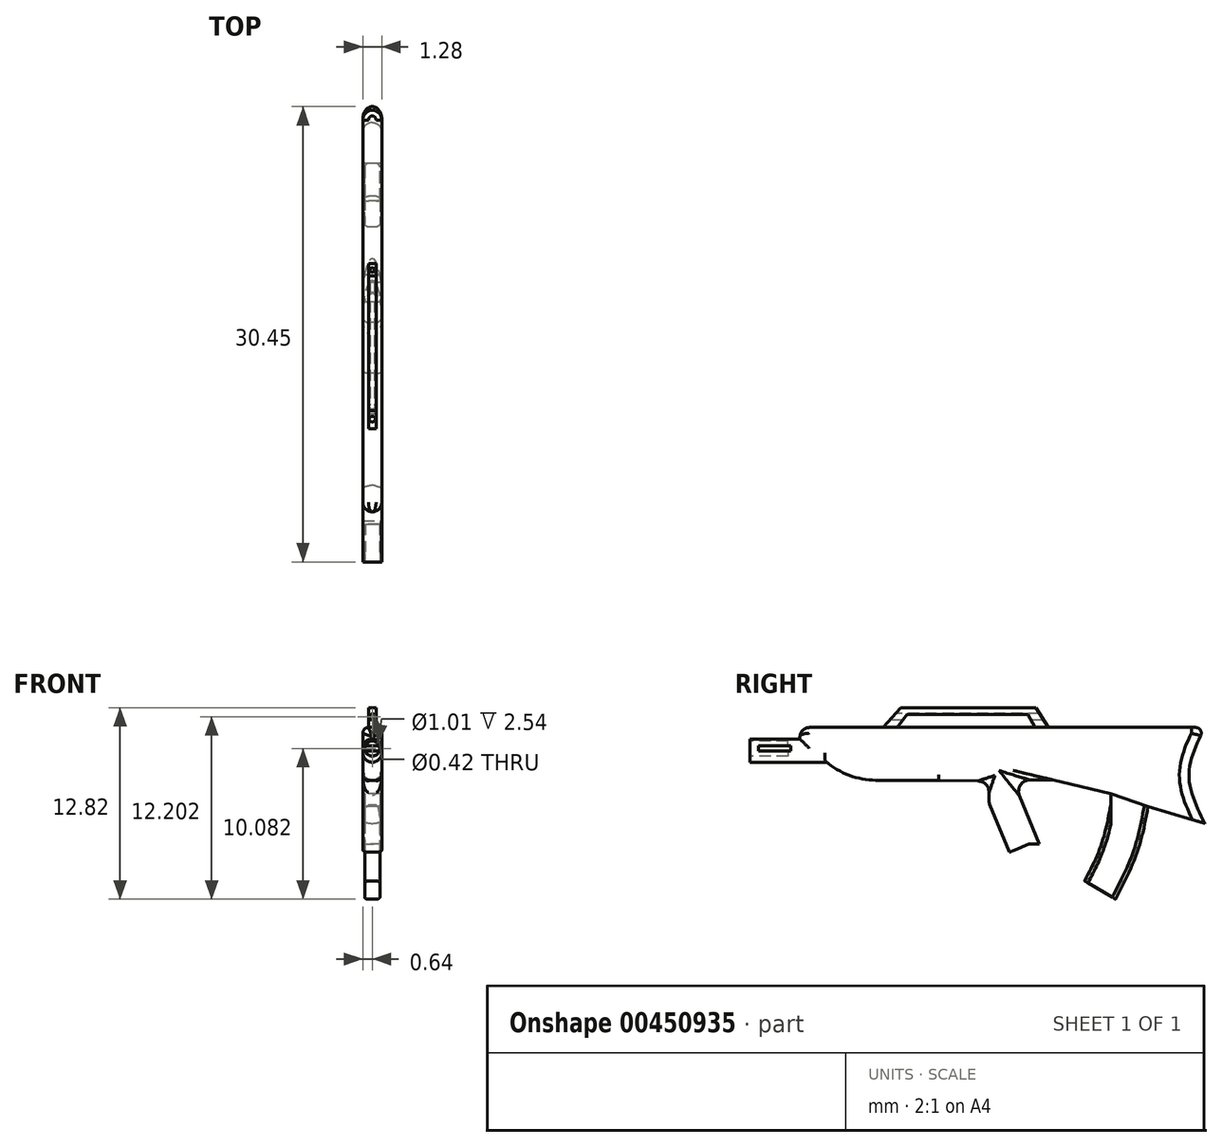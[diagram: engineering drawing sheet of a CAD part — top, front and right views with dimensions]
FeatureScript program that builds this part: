
annotation { "Feature Type Name" : "Feature", "Feature Type Description" : "" }
export const myFeature = defineFeature(function(context is Context, id is Id, definition is map)
    precondition{}
    {
        {
            var Q0;
            Q0=qCreatedBy(makeId("Right.planeOp"),FACE);
            var sketch = newSketch(context, id + "F0", { "sketchPlane" : qUnion([Q0])});
            skLineSegment(sketch, "E0", {"start": v(0, 0) * mm, "end": v(27.1, 0) * mm});
            skFitSpline(sketch, "E1", {"points": [v(27.1, 0) * mm, v(26.04, -3.17) * mm, v(27.1, -6.42) * mm], "startDerivative": vector(-3.2, -6.36) * mm, "endDerivative": vector(3.2, -6.47) * mm});
            skLineSegment(sketch, "E2", {"start": v(27.1, -6.42) * mm, "end": v(23.3, -5.3) * mm});
            skFitSpline(sketch, "E3", {"points": [v(23.3, -5.3) * mm, v(22.6, -8.28) * mm, v(21.12, -11.49) * mm], "startDerivative": vector(-1.13, -6.19) * mm, "endDerivative": vector(-3.2, -6.2) * mm});
            skLineSegment(sketch, "E4", {"start": v(0, 0) * mm, "end": v(0, -0.77) * mm});
            skLineSegment(sketch, "E5", {"start": v(0, -0.77) * mm, "end": v(-3.35, -0.77) * mm});
            skLineSegment(sketch, "E6", {"start": v(-3.35, -0.77) * mm, "end": v(-3.35, -1.64) * mm});
            skLineSegment(sketch, "E7", {"start": v(-3.35, -1.64) * mm, "end": v(-3.35, -2.33) * mm});
            skLineSegment(sketch, "E8", {"start": v(-3.35, -2.33) * mm, "end": v(0, -2.33) * mm});
            skLineSegment(sketch, "E9", {"start": v(0, -2.33) * mm, "end": v(0, -3.53) * mm});
            skLineSegment(sketch, "E10", {"start": v(0, -3.53) * mm, "end": v(9.29, -3.53) * mm});
            skLineSegment(sketch, "E11", {"start": v(9.29, -3.53) * mm, "end": v(10.23, -5.06) * mm});
            skLineSegment(sketch, "E12", {"start": v(10.23, -5.06) * mm, "end": v(12.67, -5.06) * mm});
            skLineSegment(sketch, "E13", {"start": v(12.67, -5.06) * mm, "end": v(12.67, -3.58) * mm});
            skLineSegment(sketch, "E14", {"start": v(12.67, -3.58) * mm, "end": v(9.29, -3.53) * mm});
            skLineSegment(sketch, "E15", {"start": v(12.67, -5.06) * mm, "end": v(14.02, -8.34) * mm});
            skLineSegment(sketch, "E16", {"start": v(14.02, -8.34) * mm, "end": v(15.35, -7.8) * mm});
            skLineSegment(sketch, "E17", {"start": v(15.35, -7.8) * mm, "end": v(13.58, -3.51) * mm});
            skLineSegment(sketch, "E18", {"start": v(13.58, -3.51) * mm, "end": v(12.67, -3.58) * mm});
            skLineSegment(sketch, "E19", {"start": v(21.12, -11.49) * mm, "end": v(19.06, -10.27) * mm});
            skFitSpline(sketch, "E20", {"points": [v(19.06, -10.27) * mm, v(20.18, -7.83) * mm, v(20.8, -5.2) * mm], "startDerivative": vector(2.5, 4.8) * mm, "endDerivative": vector(1, 5.35) * mm});
            skLineSegment(sketch, "E21", {"start": v(13.58, -3.51) * mm, "end": v(16.95, -3.51) * mm});
            skLineSegment(sketch, "E22", {"start": v(16.95, -3.51) * mm, "end": v(20.8, -4.43) * mm});
            skLineSegment(sketch, "E23", {"start": v(20.8, -4.43) * mm, "end": v(20.8, -5.2) * mm});
            skLineSegment(sketch, "E24", {"start": v(14.26, -3.51) * mm, "end": v(16, -7.8) * mm});
            skLineSegment(sketch, "E25", {"start": v(16, -7.8) * mm, "end": v(15.35, -7.8) * mm});
            skLineSegment(sketch, "E26", {"start": v(16.62, 0) * mm, "end": v(15.8, 1.33) * mm});
            skLineSegment(sketch, "E27", {"start": v(15.8, 1.33) * mm, "end": v(6.75, 1.33) * mm});
            skLineSegment(sketch, "E28", {"start": v(6.75, 1.33) * mm, "end": v(5.57, 0) * mm});
            skLineSegment(sketch, "E29", {"start": v(0.72, 0) * mm, "end": v(0.72, 1.2) * mm});
            skLineSegment(sketch, "E30", {"start": v(0.72, 1.2) * mm, "end": v(0.72, 1.86) * mm});
            skLineSegment(sketch, "E31", {"start": v(0.72, 1.86) * mm, "end": v(2.07, 0) * mm});
            skLineSegment(sketch, "E32", {"start": v(20.8, -4.43) * mm, "end": v(23.3, -5.3) * mm});
            skFitSpline(sketch, "E33", {"points": [v(11.82, -3.57) * mm, v(11.61, -4.19) * mm, v(11.17, -4.73) * mm, v(11.36, -4.1) * mm, v(11.35, -3.56) * mm], "startDerivative": vector(-0.42, -2.2) * mm, "endDerivative": vector(-0.44, 2) * mm});
            skLineSegment(sketch, "E34", {"start": v(12.75, -5.25) * mm, "end": v(10.16, -5.25) * mm});
            skLineSegment(sketch, "E35", {"start": v(10.16, -5.25) * mm, "end": v(9.1, -3.53) * mm});
            skLineSegment(sketch, "E36", {"start": v(6.53, 0) * mm, "end": v(7.15, 0.87) * mm});
            skLineSegment(sketch, "E37", {"start": v(7.15, 0.87) * mm, "end": v(15.25, 0.87) * mm});
            skLineSegment(sketch, "E38", {"start": v(15.25, 0.87) * mm, "end": v(15.73, 0) * mm});
            skSolve(sketch);
        }
        {
            var Q0;
            {var subQ18=sQuery(id+"F0.wireOp",EDGE,"E1");Q0=makeQuery(id+"F0.imprint","IMPRINT",FACE,{"disambiguationData":[TD([[makeQuery(id+"F0.imprint","IMPRINT",EDGE,{"derivedFrom":subQ18}),-1.0]])]});}
            var Q1;
            {var subQ0=sQuery(id+"F0.wireOp",EDGE,"E17");Q1=makeQuery(id+"F0.imprint","IMPRINT",FACE,{"disambiguationData":[TD([[makeQuery(id+"F0.imprint","IMPRINT",EDGE,{"derivedFrom":subQ0}),-1.0]])]});}
            var Q2;
            {var subQ2=sQuery(id+"F0.wireOp",EDGE,"E13");Q2=makeQuery(id+"F0.imprint","IMPRINT",FACE,{"disambiguationData":[TD([[makeQuery(id+"F0.imprint","IMPRINT",EDGE,{"derivedFrom":subQ2}),-1.0]])]});}
            extrude(context, id + "F1", {"entities" : qUnion([Q0, Q1, Q2]), "depth" : 0.64 * mm});
        }
        {
            var Q0;
            {var subQ18=sQuery(id+"F0.wireOp",EDGE,"E1");Q0=makeQuery(id+"F0.imprint","IMPRINT",FACE,{"disambiguationData":[TD([[makeQuery(id+"F0.imprint","IMPRINT",EDGE,{"derivedFrom":subQ18}),-1.0]])]});}
            var Q1;
            {var subQ0=sQuery(id+"F0.wireOp",EDGE,"E17");Q1=makeQuery(id+"F0.imprint","IMPRINT",FACE,{"disambiguationData":[TD([[makeQuery(id+"F0.imprint","IMPRINT",EDGE,{"derivedFrom":subQ0}),-1.0]])]});}
            var Q2;
            {var subQ2=sQuery(id+"F0.wireOp",EDGE,"E13");Q2=makeQuery(id+"F0.imprint","IMPRINT",FACE,{"disambiguationData":[TD([[makeQuery(id+"F0.imprint","IMPRINT",EDGE,{"derivedFrom":subQ2}),-1.0]])]});}
            extrude(context, id + "F2", {"entities" : qUnion([Q0, Q1, Q2]), "operationType" : NewBodyOperationType.ADD, "oppositeDirection" : true, "depth" : 0.64 * mm});
        }
        {
            var Q0;
            Q0=makeQuery(id+"F2.opExtrude","CAP_EDGE",EDGE,{"disambiguationData":[OSD([sQuery(id+"F0.wireOp",EDGE,"E5")])],"isStart":false});
            var Q1;
            Q1=makeQuery(id+"F1.opExtrude","CAP_EDGE",EDGE,{"disambiguationData":[OSD([sQuery(id+"F0.wireOp",EDGE,"E5")])],"isStart":false});
            var Q2;
            Q2=makeQuery(id+"F1.opExtrude","CAP_EDGE",EDGE,{"disambiguationData":[OSD([sQuery(id+"F0.wireOp",EDGE,"E8")])],"isStart":false});
            var Q3;
            Q3=makeQuery(id+"F2.opExtrude","CAP_EDGE",EDGE,{"disambiguationData":[OSD([sQuery(id+"F0.wireOp",EDGE,"E8")])],"isStart":false});
            fillet(context, id + "F3", {"entities" : qUnion([Q0, Q1, Q2, Q3]), "radius" : 0.64 * mm, "tangentPropagation" : true, "allowEdgeOverflow" : false});
        }
        {
            var Q0;
            {var subQ0=sQuery(id+"F0.wireOp",EDGE,"E10");var subQ1=sQuery(id+"F0.wireOp",EDGE,"E9");Q0=makeQuery(id+"F2.boolean.opBoolean","MERGE",EDGE,{"derivedFrom":[makeQuery(id+"F1.opExtrude","SWEPT_EDGE",EDGE,{"disambiguationData":[OSD([subQ1,subQ0])]}),makeQuery(id+"F2.opExtrude","SWEPT_EDGE",EDGE,{"disambiguationData":[OSD([subQ1,subQ0])]})]});}
            fillet(context, id + "F4", {"entities" : qUnion([Q0]), "radius" : 5.08 * mm, "tangentPropagation" : true, "allowEdgeOverflow" : false});
        }
        {
            var Q0;
            Q0=makeQuery(id+"F2.opExtrude","CAP_EDGE",EDGE,{"disambiguationData":[OSD([sQuery(id+"F0.wireOp",EDGE,"E24")])],"isStart":false});
            var Q1;
            Q1=makeQuery(id+"F1.opExtrude","CAP_EDGE",EDGE,{"disambiguationData":[OSD([sQuery(id+"F0.wireOp",EDGE,"E24")])],"isStart":false});
            var Q2;
            Q2=makeQuery(id+"F2.opExtrude","CAP_EDGE",EDGE,{"disambiguationData":[OSD([sQuery(id+"F0.wireOp",EDGE,"E1")])],"isStart":false});
            var Q3;
            Q3=makeQuery(id+"F1.opExtrude","CAP_EDGE",EDGE,{"disambiguationData":[OSD([sQuery(id+"F0.wireOp",EDGE,"E1")])],"isStart":false});
            var Q4;
            {var subQ0=sQuery(id+"F0.wireOp",EDGE,"E4");var subQ1=sQuery(id+"F0.wireOp",EDGE,"E0");Q4=makeQuery(id+"F2.boolean.opBoolean","MERGE",EDGE,{"derivedFrom":[makeQuery(id+"F1.opExtrude","SWEPT_EDGE",EDGE,{"disambiguationData":[OSD([subQ1,subQ0])]}),makeQuery(id+"F2.opExtrude","SWEPT_EDGE",EDGE,{"disambiguationData":[OSD([subQ1,subQ0])]})]});}
            var Q5;
            Q5=makeQuery(id+"F1.opExtrude","CAP_EDGE",EDGE,{"disambiguationData":[OSD([sQuery(id+"F0.wireOp",EDGE,"E4")])],"isStart":false});
            var Q6;
            Q6=makeQuery(id+"F2.opExtrude","CAP_EDGE",EDGE,{"disambiguationData":[OSD([sQuery(id+"F0.wireOp",EDGE,"E4")])],"isStart":false});
            var Q7;
            Q7=makeQuery(id+"F1.opExtrude","CAP_EDGE",EDGE,{"disambiguationData":[OSD([sQuery(id+"F0.wireOp",EDGE,"E21")])],"isStart":false});
            var Q8;
            Q8=makeQuery(id+"F2.opExtrude","CAP_EDGE",EDGE,{"disambiguationData":[OSD([sQuery(id+"F0.wireOp",EDGE,"E21")])],"isStart":false});
            fillet(context, id + "F5", {"entities" : qUnion([Q0, Q1, Q2, Q3, Q4, Q5, Q6, Q7, Q8]), "radius" : 0.64 * mm, "tangentPropagation" : true, "allowEdgeOverflow" : false});
        }
        {
            var Q0;
            Q0=makeQuery(id+"F0.imprint","IMPRINT",FACE,{"disambiguationData":[TD([[makeQuery(id+"F0.imprint","IMPRINT",EDGE,{"derivedFrom":sQuery(id+"F0.wireOp",EDGE,"E3")}),-1.0]])]});
            extrude(context, id + "F6", {"entities" : qUnion([Q0]), "operationType" : NewBodyOperationType.ADD, "depth" : 0.5 * mm});
        }
        {
            var Q0;
            Q0=makeQuery(id+"F0.imprint","IMPRINT",FACE,{"disambiguationData":[TD([[makeQuery(id+"F0.imprint","IMPRINT",EDGE,{"derivedFrom":sQuery(id+"F0.wireOp",EDGE,"E3")}),-1.0]])]});
            extrude(context, id + "F7", {"entities" : qUnion([Q0]), "operationType" : NewBodyOperationType.ADD, "oppositeDirection" : true, "depth" : 0.5 * mm});
        }
        {
            var Q0;
            Q0=makeQuery(id+"F2.opExtrude","CAP_EDGE",EDGE,{"disambiguationData":[OSD([sQuery(id+"F0.wireOp",EDGE,"E13")])],"isStart":false});
            var Q1;
            Q1=makeQuery(id+"F2.opExtrude","CAP_EDGE",EDGE,{"disambiguationData":[OSD([sQuery(id+"F0.wireOp",EDGE,"E15")])],"isStart":false});
            var Q2;
            Q2=makeQuery(id+"F1.opExtrude","CAP_EDGE",EDGE,{"disambiguationData":[OSD([sQuery(id+"F0.wireOp",EDGE,"E15")])],"isStart":false});
            var Q3;
            Q3=makeQuery(id+"F1.opExtrude","CAP_EDGE",EDGE,{"disambiguationData":[OSD([sQuery(id+"F0.wireOp",EDGE,"E13")])],"isStart":false});
            var Q4;
            {var subQ0=sQuery(id+"F0.wireOp",EDGE,"E15");var subQ1=sQuery(id+"F0.wireOp",EDGE,"E13");var subQ2=sQuery(id+"F0.wireOp",EDGE,"E12");Q4=makeQuery(id+"F2.boolean.opBoolean","MERGE",EDGE,{"derivedFrom":[makeQuery(id+"F1.opExtrude","SWEPT_EDGE",EDGE,{"disambiguationData":[OSD([subQ2,subQ1,subQ0])]}),makeQuery(id+"F2.opExtrude","SWEPT_EDGE",EDGE,{"disambiguationData":[OSD([subQ2,subQ1,subQ0])]})]});}
            var Q5;
            Q5=makeQuery(id+"F1.opExtrude","CAP_EDGE",EDGE,{"disambiguationData":[OSD([sQuery(id+"F0.wireOp",EDGE,"E14")])],"isStart":false});
            var Q6;
            Q6=makeQuery(id+"F2.opExtrude","CAP_EDGE",EDGE,{"disambiguationData":[OSD([sQuery(id+"F0.wireOp",EDGE,"E14")])],"isStart":false});
            var Q7;
            {var subQ0=sQuery(id+"F0.wireOp",EDGE,"E10");var subQ1=sQuery(id+"F0.wireOp",EDGE,"E9");Q7=makeQuery(id+"F4.opFillet","BLEND_EDGE",EDGE,{"blendedFrom":[makeQuery(id+"F2.boolean.opBoolean","MERGE",EDGE,{"derivedFrom":[makeQuery(id+"F1.opExtrude","SWEPT_EDGE",EDGE,{"disambiguationData":[OSD([subQ1,subQ0])]}),makeQuery(id+"F2.opExtrude","SWEPT_EDGE",EDGE,{"disambiguationData":[OSD([subQ1,subQ0])]})]}),makeQuery(id+"F1.opExtrude","CAP_FACE",FACE,{"disambiguationData":[OSD([sQuery(id+"F0.wireOp",EDGE,"E0"),sQuery(id+"F0.wireOp",EDGE,"E1"),sQuery(id+"F0.wireOp",EDGE,"E2"),sQuery(id+"F0.wireOp",EDGE,"E4"),sQuery(id+"F0.wireOp",EDGE,"E5"),sQuery(id+"F0.wireOp",EDGE,"E6"),sQuery(id+"F0.wireOp",EDGE,"E7"),sQuery(id+"F0.wireOp",EDGE,"E8"),subQ1,subQ0,sQuery(id+"F0.wireOp",EDGE,"E13"),sQuery(id+"F0.wireOp",EDGE,"E14"),sQuery(id+"F0.wireOp",EDGE,"E15"),sQuery(id+"F0.wireOp",EDGE,"E16"),sQuery(id+"F0.wireOp",EDGE,"E21"),sQuery(id+"F0.wireOp",EDGE,"E22"),sQuery(id+"F0.wireOp",EDGE,"E24"),sQuery(id+"F0.wireOp",EDGE,"E25"),sQuery(id+"F0.wireOp",EDGE,"E32")])],"isStart":false})],"blendedInto":[makeQuery(id+"F1.opExtrude","CAP_FACE",FACE,{"disambiguationData":[OSD([sQuery(id+"F0.wireOp",EDGE,"E0"),sQuery(id+"F0.wireOp",EDGE,"E1"),sQuery(id+"F0.wireOp",EDGE,"E2"),sQuery(id+"F0.wireOp",EDGE,"E4"),sQuery(id+"F0.wireOp",EDGE,"E5"),sQuery(id+"F0.wireOp",EDGE,"E6"),sQuery(id+"F0.wireOp",EDGE,"E7"),sQuery(id+"F0.wireOp",EDGE,"E8"),subQ1,subQ0,sQuery(id+"F0.wireOp",EDGE,"E13"),sQuery(id+"F0.wireOp",EDGE,"E14"),sQuery(id+"F0.wireOp",EDGE,"E15"),sQuery(id+"F0.wireOp",EDGE,"E16"),sQuery(id+"F0.wireOp",EDGE,"E21"),sQuery(id+"F0.wireOp",EDGE,"E22"),sQuery(id+"F0.wireOp",EDGE,"E24"),sQuery(id+"F0.wireOp",EDGE,"E25"),sQuery(id+"F0.wireOp",EDGE,"E32")])],"isStart":false})]});}
            var Q8;
            {var subQ0=sQuery(id+"F0.wireOp",EDGE,"E10");var subQ1=sQuery(id+"F0.wireOp",EDGE,"E9");Q8=makeQuery(id+"F4.opFillet","BLEND_EDGE",EDGE,{"blendedFrom":[makeQuery(id+"F2.boolean.opBoolean","MERGE",EDGE,{"derivedFrom":[makeQuery(id+"F1.opExtrude","SWEPT_EDGE",EDGE,{"disambiguationData":[OSD([subQ1,subQ0])]}),makeQuery(id+"F2.opExtrude","SWEPT_EDGE",EDGE,{"disambiguationData":[OSD([subQ1,subQ0])]})]}),makeQuery(id+"F2.opExtrude","CAP_FACE",FACE,{"disambiguationData":[OSD([sQuery(id+"F0.wireOp",EDGE,"E0"),sQuery(id+"F0.wireOp",EDGE,"E1"),sQuery(id+"F0.wireOp",EDGE,"E2"),sQuery(id+"F0.wireOp",EDGE,"E4"),sQuery(id+"F0.wireOp",EDGE,"E5"),sQuery(id+"F0.wireOp",EDGE,"E6"),sQuery(id+"F0.wireOp",EDGE,"E7"),sQuery(id+"F0.wireOp",EDGE,"E8"),subQ1,subQ0,sQuery(id+"F0.wireOp",EDGE,"E13"),sQuery(id+"F0.wireOp",EDGE,"E14"),sQuery(id+"F0.wireOp",EDGE,"E15"),sQuery(id+"F0.wireOp",EDGE,"E16"),sQuery(id+"F0.wireOp",EDGE,"E21"),sQuery(id+"F0.wireOp",EDGE,"E22"),sQuery(id+"F0.wireOp",EDGE,"E24"),sQuery(id+"F0.wireOp",EDGE,"E25"),sQuery(id+"F0.wireOp",EDGE,"E32")])],"isStart":false})],"blendedInto":[makeQuery(id+"F2.opExtrude","CAP_FACE",FACE,{"disambiguationData":[OSD([sQuery(id+"F0.wireOp",EDGE,"E0"),sQuery(id+"F0.wireOp",EDGE,"E1"),sQuery(id+"F0.wireOp",EDGE,"E2"),sQuery(id+"F0.wireOp",EDGE,"E4"),sQuery(id+"F0.wireOp",EDGE,"E5"),sQuery(id+"F0.wireOp",EDGE,"E6"),sQuery(id+"F0.wireOp",EDGE,"E7"),sQuery(id+"F0.wireOp",EDGE,"E8"),subQ1,subQ0,sQuery(id+"F0.wireOp",EDGE,"E13"),sQuery(id+"F0.wireOp",EDGE,"E14"),sQuery(id+"F0.wireOp",EDGE,"E15"),sQuery(id+"F0.wireOp",EDGE,"E16"),sQuery(id+"F0.wireOp",EDGE,"E21"),sQuery(id+"F0.wireOp",EDGE,"E22"),sQuery(id+"F0.wireOp",EDGE,"E24"),sQuery(id+"F0.wireOp",EDGE,"E25"),sQuery(id+"F0.wireOp",EDGE,"E32")])],"isStart":false})]});}
            fillet(context, id + "F8", {"entities" : qUnion([Q0, Q1, Q2, Q3, Q4, Q5, Q6, Q7, Q8]), "radius" : 0.38 * mm, "tangentPropagation" : true, "allowEdgeOverflow" : false});
        }
        {
            var Q0;
            {var subQ0=sQuery(id+"F0.wireOp",EDGE,"E18");var subQ1=sQuery(id+"F0.wireOp",EDGE,"E14");var subQ2=sQuery(id+"F0.wireOp",EDGE,"E13");Q0=makeQuery(id+"F2.boolean.opBoolean","MERGE",EDGE,{"derivedFrom":[makeQuery(id+"F1.opExtrude","SWEPT_EDGE",EDGE,{"disambiguationData":[OSD([subQ2,subQ1,subQ0])]}),makeQuery(id+"F2.opExtrude","SWEPT_EDGE",EDGE,{"disambiguationData":[OSD([subQ2,subQ1,subQ0])]})]});}
            var Q1;
            Q1=makeQuery(id+"F5.opFillet","BLEND_EDGE",EDGE,{"blendedFrom":[makeQuery(id+"F1.opExtrude","CAP_EDGE",EDGE,{"disambiguationData":[OSD([sQuery(id+"F0.wireOp",EDGE,"E21")])],"isStart":false}),makeQuery(id+"F1.opExtrude","CAP_EDGE",EDGE,{"disambiguationData":[OSD([sQuery(id+"F0.wireOp",EDGE,"E24")])],"isStart":false})],"blendedInto":[]});
            fillet(context, id + "F9", {"entities" : qUnion([Q0, Q1]), "radius" : 0.76 * mm, "tangentPropagation" : true, "allowEdgeOverflow" : false});
        }
        {
            var Q0;
            Q0=makeQuery(id+"F6.opExtrude","CAP_EDGE",EDGE,{"disambiguationData":[OSD([sQuery(id+"F0.wireOp",EDGE,"E3")])],"isStart":false});
            var Q1;
            Q1=makeQuery(id+"F6.opExtrude","CAP_EDGE",EDGE,{"disambiguationData":[OSD([sQuery(id+"F0.wireOp",EDGE,"E20")])],"isStart":false});
            var Q2;
            Q2=makeQuery(id+"F7.opExtrude","CAP_EDGE",EDGE,{"disambiguationData":[OSD([sQuery(id+"F0.wireOp",EDGE,"E20")])],"isStart":false});
            var Q3;
            Q3=makeQuery(id+"F7.opExtrude","CAP_EDGE",EDGE,{"disambiguationData":[OSD([sQuery(id+"F0.wireOp",EDGE,"E3")])],"isStart":false});
            fillet(context, id + "F10", {"entities" : qUnion([Q0, Q1, Q2, Q3]), "radius" : 0.25 * mm, "tangentPropagation" : true, "allowEdgeOverflow" : false});
        }
        {
            var Q0;
            Q0=makeQuery(id+"F2.opExtrude","CAP_EDGE",EDGE,{"disambiguationData":[OSD([sQuery(id+"F0.wireOp",EDGE,"E0")])],"isStart":false});
            var Q1;
            Q1=makeQuery(id+"F1.opExtrude","CAP_EDGE",EDGE,{"disambiguationData":[OSD([sQuery(id+"F0.wireOp",EDGE,"E0")])],"isStart":false});
            fillet(context, id + "F11", {"entities" : qUnion([Q0, Q1]), "radius" : 0.38 * mm, "tangentPropagation" : true, "allowEdgeOverflow" : false});
        }
        {
            var Q0;
            {var subQ0=sQuery(id+"F0.wireOp",EDGE,"E7");var subQ1=sQuery(id+"F0.wireOp",EDGE,"E6");Q0=makeQuery(id+"F2.boolean.opBoolean","MERGE",FACE,{"derivedFrom":[makeQuery(id+"F1.opExtrude","SWEPT_FACE",FACE,{"disambiguationData":[OSD([subQ1,subQ0])]}),makeQuery(id+"F2.opExtrude","SWEPT_FACE",FACE,{"disambiguationData":[OSD([subQ1,subQ0])]})]});}
            var sketch = newSketch(context, id + "F12", { "sketchPlane" : qUnion([Q0])});
            skCircle(sketch, "E39", {"center": v(0, -1.4) * mm, "radius": 0.5 * mm});
            skSolve(sketch);
        }
        {
            var Q0;
            Q0=makeQuery(id+"F12.imprint","IMPRINT",FACE,{"disambiguationData":[TD([[makeQuery(id+"F12.imprint","IMPRINT",EDGE,{"derivedFrom":sQuery(id+"F12.wireOp",EDGE,"E39")}),1.0]])]});
            extrude(context, id + "F13", {"entities" : qUnion([Q0]), "operationType" : NewBodyOperationType.REMOVE, "oppositeDirection" : true, "depth" : 2.54 * mm});
        }
        {
            var Q0;
            Q0=makeQuery(id+"F1.opExtrude","CAP_FACE",FACE,{"disambiguationData":[OSD([sQuery(id+"F0.wireOp",EDGE,"E0"),sQuery(id+"F0.wireOp",EDGE,"E1"),sQuery(id+"F0.wireOp",EDGE,"E2"),sQuery(id+"F0.wireOp",EDGE,"E4"),sQuery(id+"F0.wireOp",EDGE,"E5"),sQuery(id+"F0.wireOp",EDGE,"E6"),sQuery(id+"F0.wireOp",EDGE,"E7"),sQuery(id+"F0.wireOp",EDGE,"E8"),sQuery(id+"F0.wireOp",EDGE,"E9"),sQuery(id+"F0.wireOp",EDGE,"E10"),sQuery(id+"F0.wireOp",EDGE,"E13"),sQuery(id+"F0.wireOp",EDGE,"E14"),sQuery(id+"F0.wireOp",EDGE,"E15"),sQuery(id+"F0.wireOp",EDGE,"E16"),sQuery(id+"F0.wireOp",EDGE,"E21"),sQuery(id+"F0.wireOp",EDGE,"E22"),sQuery(id+"F0.wireOp",EDGE,"E24"),sQuery(id+"F0.wireOp",EDGE,"E25"),sQuery(id+"F0.wireOp",EDGE,"E32")])],"isStart":false});
            var sketch = newSketch(context, id + "F14", { "sketchPlane" : qUnion([Q0])});
            skLineSegment(sketch, "E40.bottom", {"start": v(-0.6, -1.23) * mm, "end": v(-2.78, -1.23) * mm});
            skLineSegment(sketch, "E40.top", {"start": v(-0.6, -1.59) * mm, "end": v(-2.78, -1.59) * mm});
            skLineSegment(sketch, "E40.left", {"start": v(-0.6, -1.23) * mm, "end": v(-0.6, -1.59) * mm});
            skLineSegment(sketch, "E40.right", {"start": v(-2.78, -1.23) * mm, "end": v(-2.78, -1.59) * mm});
            skPoint(sketch, "E40.middle", {"position": v(-1.7, -1.4) * mm});
            skSolve(sketch);
        }
        {
            var Q0;
            {var subQ0=sQuery(id+"F14.wireOp",EDGE,"E40.top");Q0=makeQuery(id+"F14.imprint","IMPRINT",FACE,{"disambiguationData":[TD([[makeQuery(id+"F14.imprint","IMPRINT",EDGE,{"derivedFrom":subQ0}),-1.0]])]});}
            var Q1;
            {var subQ0=sQuery(id+"F14.wireOp",EDGE,"E40.bottom");Q1=makeQuery(id+"F14.imprint","IMPRINT",FACE,{"disambiguationData":[TD([[makeQuery(id+"F14.imprint","IMPRINT",EDGE,{"derivedFrom":subQ0}),1.0]])]});}
            extrude(context, id + "F15", {"entities" : qUnion([Q0, Q1]), "operationType" : NewBodyOperationType.REMOVE, "oppositeDirection" : true, "depth" : 25.4 * mm});
        }
        {
            var Q0;
            {var subQ0=sQuery(id+"F0.wireOp",EDGE,"E26");Q0=makeQuery(id+"F0.imprint","IMPRINT",FACE,{"disambiguationData":[TD([[makeQuery(id+"F0.imprint","IMPRINT",EDGE,{"derivedFrom":subQ0}),1.0]])]});}
            extrude(context, id + "F16", {"entities" : qUnion([Q0]), "operationType" : NewBodyOperationType.ADD, "depth" : 0.25 * mm});
        }
        {
            var Q0;
            {var subQ0=sQuery(id+"F0.wireOp",EDGE,"E26");Q0=makeQuery(id+"F0.imprint","IMPRINT",FACE,{"disambiguationData":[TD([[makeQuery(id+"F0.imprint","IMPRINT",EDGE,{"derivedFrom":subQ0}),1.0]])]});}
            extrude(context, id + "F17", {"entities" : qUnion([Q0]), "operationType" : NewBodyOperationType.ADD, "oppositeDirection" : true, "depth" : 0.25 * mm});
        }
        {
            var Q0;
            Q0=qCreatedBy(makeId("Front.planeOp"),FACE);
            var sketch = newSketch(context, id + "F18", { "sketchPlane" : qUnion([Q0])});
            skCircle(sketch, "E41", {"center": v(0, 0.71) * mm, "radius": 0.21 * mm});
            skSolve(sketch);
        }
        {
            var Q0;
            Q0=makeQuery(id+"F18.imprint","IMPRINT",FACE,{"disambiguationData":[TD([[makeQuery(id+"F18.imprint","IMPRINT",EDGE,{"derivedFrom":sQuery(id+"F18.wireOp",EDGE,"E41")}),1.0]])]});
            extrude(context, id + "F19", {"entities" : qUnion([Q0]), "operationType" : NewBodyOperationType.REMOVE, "oppositeDirection" : true, "depth" : 25.4 * mm});
        }
    });
